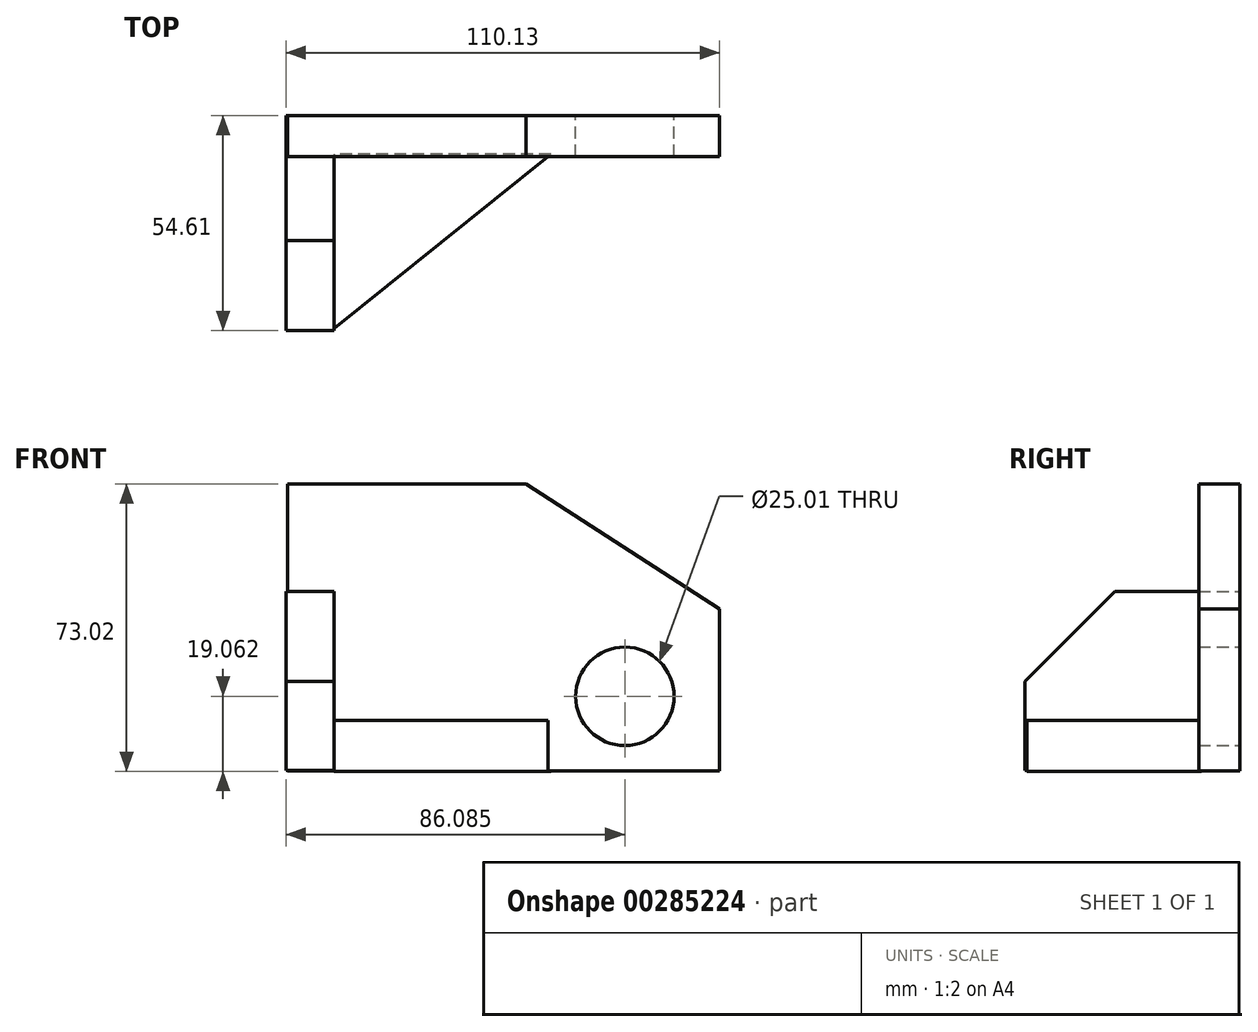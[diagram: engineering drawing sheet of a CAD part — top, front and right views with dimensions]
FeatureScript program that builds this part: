
annotation { "Feature Type Name" : "Feature", "Feature Type Description" : "" }
export const myFeature = defineFeature(function(context is Context, id is Id, definition is map)
    precondition{}
    {
        {
            var Q0;
            Q0=qCreatedBy(makeId("Front.planeOp"),FACE);
            var sketch = newSketch(context, id + "F0", { "sketchPlane" : qUnion([Q0])});
            skLineSegment(sketch, "E0", {"start": v(-55.62, 42.3) * mm, "end": v(-55.62, -30.63) * mm});
            skLineSegment(sketch, "E1", {"start": v(-55.62, -30.63) * mm, "end": v(54.17, -30.63) * mm});
            skLineSegment(sketch, "E2", {"start": v(54.17, -30.63) * mm, "end": v(54.17, 10.5) * mm});
            skLineSegment(sketch, "E3", {"start": v(54.17, 10.5) * mm, "end": v(5.01, 42.3) * mm});
            skLineSegment(sketch, "E4", {"start": v(5.01, 42.3) * mm, "end": v(-55.62, 42.3) * mm});
            skCircle(sketch, "E5", {"center": v(30.12, -11.67) * mm, "radius": 12.5 * mm});
            skSolve(sketch);
        }
        {
            var Q0;
            Q0 = qSketchRegion(id + "F0", true);
            extrude(context, id + "F1", {"entities" : qUnion([Q0]), "depth" : 10.4 * mm});
        }
        {
            var Q0;
            Q0=qCreatedBy(makeId("Front.planeOp"),FACE);
            var sketch = newSketch(context, id + "F2", { "sketchPlane" : qUnion([Q0])});
            skLineSegment(sketch, "E6.left", {"start": v(-55.96, 15.01) * mm, "end": v(-55.96, -30.46) * mm});
            skLineSegment(sketch, "E7", {"start": v(-55.96, -30.46) * mm, "end": v(-43.72, -30.46) * mm});
            skLineSegment(sketch, "E8", {"start": v(-43.72, -30.46) * mm, "end": v(-43.72, 15.01) * mm});
            skLineSegment(sketch, "E9", {"start": v(-43.72, 15.01) * mm, "end": v(-55.96, 15.01) * mm});
            skSolve(sketch);
        }
        {
            var Q0;
            Q0 = qSketchRegion(id + "F2", true);
            extrude(context, id + "F3", {"entities" : qUnion([Q0]), "operationType" : NewBodyOperationType.ADD, "depth" : 54.6 * mm});
        }
        {
            var Q0;
            Q0=makeQuery(id+"F3.opExtrude","CAP_EDGE",EDGE,{"disambiguationData":[OSD([sQuery(id+"F2.wireOp",EDGE,"E6.bottom")])],"isStart":false});
            var Q1;
            Q1=makeQuery(id+"F3.opExtrude","CAP_EDGE",EDGE,{"disambiguationData":[OSD([sQuery(id+"F2.wireOp",EDGE,"E9")])],"isStart":false});
            chamfer(context, id + "F4", {"entities" : qUnion([Q0, Q1]), "width" : 22.86 * mm, "tangentPropagation" : true});
        }
        {
            var Q0;
            Q0=qCreatedBy(makeId("Top.planeOp"),FACE);
            var sketch = newSketch(context, id + "F5", { "sketchPlane" : qUnion([Q0])});
            skLineSegment(sketch, "E10", {"start": v(-43.72, -9.76) * mm, "end": v(-43.72, -54.07) * mm});
            skLineSegment(sketch, "E11", {"start": v(-43.72, -54.07) * mm, "end": v(11.37, -9.76) * mm});
            skLineSegment(sketch, "E12", {"start": v(11.37, -9.76) * mm, "end": v(-43.72, -9.76) * mm});
            skSolve(sketch);
        }
        {
            var Q0;
            Q0 = qSketchRegion(id + "F5", true);
            extrude(context, id + "F6", {"entities" : qUnion([Q0]), "operationType" : NewBodyOperationType.ADD, "oppositeDirection" : true, "depth" : 30.73 * mm});
        }
        {
            var Q0;
            Q0=qCreatedBy(makeId("Top.planeOp"),FACE);
            var sketch = newSketch(context, id + "F7", { "sketchPlane" : qUnion([Q0])});
            skLineSegment(sketch, "E13", {"start": v(-43.72, -10.35) * mm, "end": v(-43.72, -55.23) * mm});
            skLineSegment(sketch, "E14", {"start": v(-43.72, -55.23) * mm, "end": v(11.37, -10.35) * mm});
            skLineSegment(sketch, "E15", {"start": v(11.37, -10.35) * mm, "end": v(-43.72, -10.35) * mm});
            skSolve(sketch);
        }
        {
            var Q0;
            Q0 = qSketchRegion(id + "F7", true);
            extrude(context, id + "F8", {"entities" : qUnion([Q0]), "operationType" : NewBodyOperationType.REMOVE, "oppositeDirection" : true, "depth" : 17.78 * mm});
        }
        {
            var Q0;
            Q0=qCreatedBy(makeId("Front.planeOp"),FACE);
            var sketch = newSketch(context, id + "F9", { "sketchPlane" : qUnion([Q0])});
            skLineSegment(sketch, "E16.bottom", {"start": v(-43.72, 4.23) * mm, "end": v(12.53, 4.23) * mm});
            skLineSegment(sketch, "E16.top", {"start": v(-43.72, -17.93) * mm, "end": v(12.53, -17.93) * mm});
            skLineSegment(sketch, "E16.left", {"start": v(-43.72, 4.23) * mm, "end": v(-43.72, -17.93) * mm});
            skLineSegment(sketch, "E16.right", {"start": v(12.53, 4.23) * mm, "end": v(12.53, -17.93) * mm});
            skSolve(sketch);
        }
        {
            var Q0;
            Q0 = qSketchRegion(id + "F9", true);
            extrude(context, id + "F10", {"entities" : qUnion([Q0]), "operationType" : NewBodyOperationType.ADD, "depth" : 10.4 * mm});
        }
    });
